# Revit family: DC_Rheem_PLM_Raypak_B1722ID
name_source: partatom
category: Plumbing Fixtures
revit_build: Autodesk Revit 2017 (Build: 20160225_1515(x64)
units: mm (PartAtom-declared; Revit-internal decimal feet)

## family parameters
Cut with Voids When Loaded = No
Host = Face
Part Type = Normal
Room Calculation Point = No
Round Connector Dimension = Use Radius
Shared = No

## types (4) — shared parameters
BoxHeight_ANZRS = 860 mm  [stored 2.82152 ft]
ColdWaterInletDiameter_ANZRS = 65 mm
ColdWaterInletRadius_ANZRS = 33 mm
ConnectionHeight_ANZRS = 755 mm
GasInletHeight_ANZRS = 410 mm
Height_ANZRS = 1990 mm  [stored 6.52887 ft]
HotWaterOutletDiameter_ANZRS = 65 mm
HotWaterOutletRadius_ANZRS = 33 mm
Manufacturer = Raypak
Materials_ANZRS = Raypak - Grey Powder Coated Steel
PRV_ANZRS = 15 mm  [stored 0.0492126 ft]
URL = http://www.rheem.com.au
Width_ANZRS = 825 mm  [stored 2.70669 ft]
zero-valued in all types: Default Elevation

## per-type parameters (varying)
| type | GasInletDiameter_ANZRS | GasInletRadius_ANZRS | Model | Type Comments |
| Raypak - Gas Water Heater- Indoor - 1719 MJ/h  Natural gas, modulating gas control | 50 mm  [stored 0.164042 ft] | 25 mm  [stored 0.082021 ft] | B1722NCM/ID | Recovery 6536L/h @ 50°C rise |
| Raypak - Gas Water Heater- Indoor - 1719 MJ/h  Natural gas, On/Off gas control | 50 mm  [stored 0.164042 ft] | 25 mm  [stored 0.082021 ft] | B1722NCO/ID | Recovery 6536L/h @ 50°C rise |
| Raypak - Gas Water Heater- Indoor - 1581 MJ/h  Propane gas, modulating gas control | 25 mm  [stored 0.082021 ft] | 13 mm | B1722PCM/ID | Recovery 6020L/h @ 50°C rise |
| Raypak - Gas Water Heater- Indoor - 1581 MJ/h  Propane gas, On/Off gas control | 40 mm  [stored 0.131234 ft] | 20 mm  [stored 0.0656168 ft] | B1722PCO/ID | Recovery 6020L/h @ 50°C rise |

note: column(s) folded — value = type name in every type: Description

note: [stored X ft] marks values corroborated as IEEE doubles in the binary element streams (Revit-internal decimal feet)

## geometry (parser evidence)
native form markers: Blend x4, Sweep x2
no freeform markers — native parametric forms only
